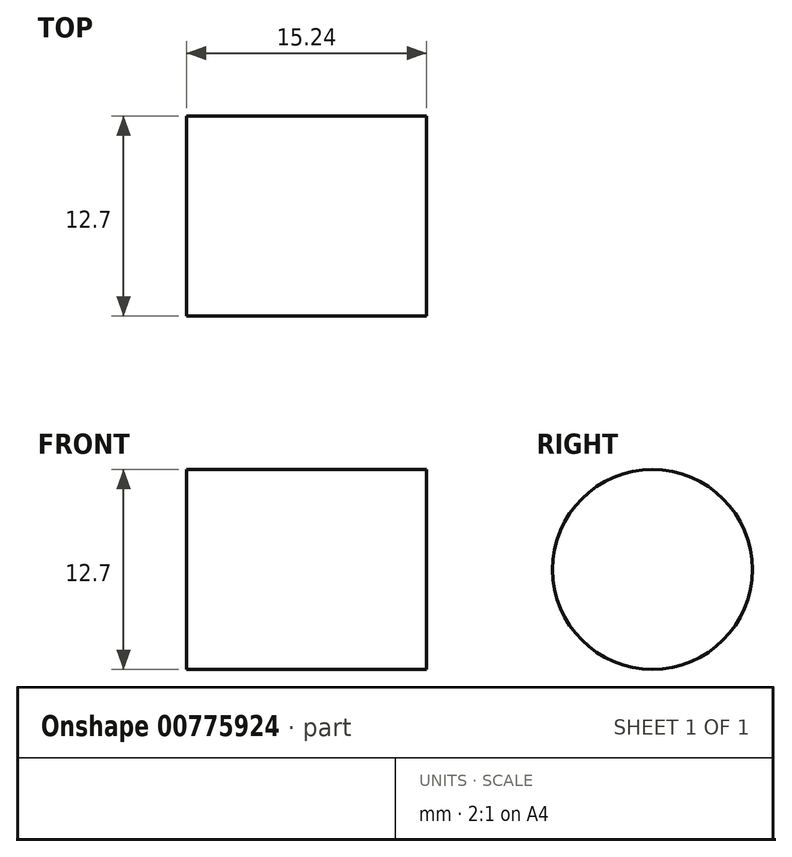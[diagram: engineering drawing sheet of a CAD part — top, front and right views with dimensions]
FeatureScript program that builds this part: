
annotation { "Feature Type Name" : "Feature", "Feature Type Description" : "" }
export const myFeature = defineFeature(function(context is Context, id is Id, definition is map)
    precondition{}
    {
        {
            var Q0;
            Q0=qCreatedBy(makeId("Right.planeOp"),FACE);
            var sketch = newSketch(context, id + "F0", { "sketchPlane" : qUnion([Q0])});
            skCircle(sketch, "E0", {"center": v(0, 0) * mm, "radius": 25.4 * mm});
            skCircle(sketch, "E1", {"center": v(0, 38.1) * mm, "radius": 12.7 * mm});
            skPoint(sketch, "E1.first.point", {"position": v(0, 25.4) * mm});
            skPoint(sketch, "E1.second.point", {"position": v(0, 50.8) * mm});
            skPoint(sketch, "E1.third.point", {"position": v(11.8, 42.8) * mm});
            skCircle(sketch, "E2", {"center": v(0, 57.15) * mm, "radius": 6.35 * mm});
            skPoint(sketch, "E2.second.point", {"position": v(0, 63.5) * mm});
            skPoint(sketch, "E2.third.point", {"position": v(5.44, 60.42) * mm});
            skSolve(sketch);
        }
        {
            var Q0;
            {var subQ0=sQuery(id+"F0.wireOp",EDGE,"E2");Q0=makeQuery(id+"F0.imprint","IMPRINT",FACE,{"disambiguationData":[TD([[makeQuery(id+"F0.imprint","IMPRINT",EDGE,{"disambiguationData":[TD([[makeQuery(id+"F0.imprint","INTERSECT",VERTEX,{"derivedFrom":[sQuery(id+"F0.wireOp",EDGE,"E1"),subQ0]}),-1.0]])],"derivedFrom":subQ0}),1.0]])]});}
            extrude(context, id + "F1", {"entities" : qUnion([Q0]), "depth" : 15.24 * mm, "offsetDistance" : 25.4 * mm});
        }
    });
